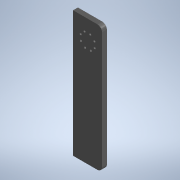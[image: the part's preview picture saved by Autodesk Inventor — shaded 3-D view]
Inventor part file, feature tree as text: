
AUTODESK INVENTOR PART (.ipt)
format: ipt  version: 2021 (Build 250183000, 183)  size: 125,440 bytes
history: native  units: mm (DEFAULTED — no unit token found)
features: sketch x3, extrude x2, fillet x1, other x1
ambient origin geometry x8: Origin, YZ Plane, XZ Plane, XY Plane, X Axis, Y Axis, Z Axis, Center Point
bodies: Solid1 (feature_tree)
feature tree (7):
  extrude  "Extrusion1"  Depth=6.35mm TaperAngle=0.0deg
  fillet  "Fillet1"  Radius=6.35mm
  extrude  "Extrusion7"  Depth=2.7178mm
  sketch  "Sketch9"  dims[d62=9.779mm d63=80.0mm d65=360.0deg d67=25.4mm d68=0.0mm d69=16.8402mm d70=8.4201mm d71=8.4201mm d86=38.1mm d87=139.7mm]
  other  "Work Axis1"
  sketch  "Sketch1"  dims[d0=165.1mm d2=6.35mm d3=0.0mm d4=6.35mm]
  sketch  "Sketch8"  dims[d60=5.08mm d61=2.7178mm]
